# Revit family: Speciality_Equipment-Cord_Reel-Hubbell_Wiring-System_HBLI45143R15
name_source: partatom
category: Specialty Equipment
revit_build: Autodesk Revit 2015 (Build: 20160512_0715(x64)
units: mm (PartAtom-declared; Revit-internal decimal feet)

## types (1)
- HBLI45143R15
    Amps = 15 A
    Assembly Code = D5090900
    Cable Material = Metal-Hubbell-Black
    Cover Material = Metal-Hubbell-Yellow
    Default Elevation = 0 "
    Description = White Industrial Reel with Yellow Portable Outlet Box
    Edition number = 1
    Electrical Connector Description = Industrial Cord Reel
    Hardware Material = Paint - Hubbell - White Texture
    Housing Material = Metal-Hubbell-Gray
    Manufacturer = Hubbell Wiring Device-Kellems
    Model = HBLI45143R15
    Product Documentation Link = https://hubbellcdn.com
    Product Guid = 758862c5-899d-4c6b-9911-95953926ba56
    Product Material = Metal-Hubbell-Black
    Product Page URL = https://www.hubbell.com
    Product data url = https://bimobject.com
    URL = http://www.hubbell-wiring.com
    Voltage = 250 V
    zz Length 1 = 12.99 "

## geometry (parser evidence)
native form markers: Blend x2, Sweep x2
no freeform markers — native parametric forms only
